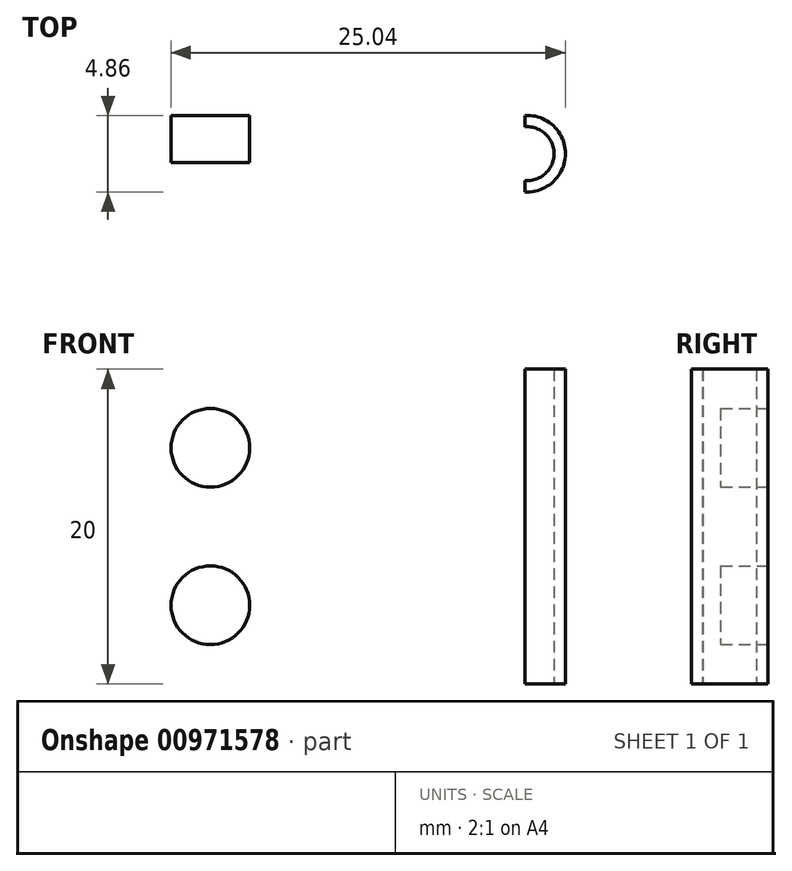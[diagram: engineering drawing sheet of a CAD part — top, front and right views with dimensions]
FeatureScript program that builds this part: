
annotation { "Feature Type Name" : "Feature", "Feature Type Description" : "" }
export const myFeature = defineFeature(function(context is Context, id is Id, definition is map)
    precondition{}
    {
        {
            var Q0;
            Q0=qCreatedBy(makeId("Top.planeOp"),FACE);
            var sketch = newSketch(context, id + "F0", { "sketchPlane" : qUnion([Q0])});
            skLineSegment(sketch, "E0", {"start": v(-27.53, 0) * mm, "end": v(-2.53, 0) * mm});
            skLineSegment(sketch, "E1", {"start": v(-27.53, 0) * mm, "end": v(-27.53, -3) * mm});
            skLineSegment(sketch, "E2", {"start": v(-27.53, -3) * mm, "end": v(-2.53, -3) * mm});
            skLineSegment(sketch, "E3", {"start": v(-2.53, -3) * mm, "end": v(-2.53, 0) * mm});
            skCircle(sketch, "E4", {"center": v(-2.67, -2.43) * mm, "radius": 2.43 * mm});
            skPoint(sketch, "E4.second.point", {"position": v(-2.53, -4.85) * mm});
            skPoint(sketch, "E4.third.point", {"position": v(-0.3, -3) * mm});
            skCircle(sketch, "E5", {"center": v(-2.67, -2.43) * mm, "radius": 1.71 * mm});
            skSolve(sketch);
        }
        {
            var Q0;
            {var subQ0=sQuery(id+"F0.wireOp",EDGE,"E4");var subQ1=sQuery(id+"F0.wireOp",EDGE,"E0");var subQ3=makeQuery(id+"F0.imprint","INTERSECT",VERTEX,{"derivedFrom":[subQ1,subQ0]});Q0=makeQuery(id+"F0.imprint","IMPRINT",FACE,{"disambiguationData":[TD([[makeQuery(id+"F0.imprint","IMPRINT",EDGE,{"disambiguationData":[TD([[subQ3,-1.0]])],"derivedFrom":subQ1}),1.0]])]});}
            var Q1;
            {var subQ0=sQuery(id+"F0.wireOp",EDGE,"E4");var subQ1=sQuery(id+"F0.wireOp",EDGE,"E2");var subQ2=makeQuery(id+"F0.imprint","INTERSECT",VERTEX,{"derivedFrom":[subQ1,subQ0]});Q1=makeQuery(id+"F0.imprint","IMPRINT",FACE,{"disambiguationData":[TD([[makeQuery(id+"F0.imprint","IMPRINT",EDGE,{"disambiguationData":[TD([[subQ2,-1.0]])],"derivedFrom":subQ1}),-1.0]])]});}
            var Q2;
            {var subQ0=sQuery(id+"F0.wireOp",EDGE,"E4");var subQ7=sQuery(id+"F0.wireOp",EDGE,"E2");var subQ8=makeQuery(id+"F0.imprint","INTERSECT",VERTEX,{"derivedFrom":[subQ7,subQ0]});Q2=makeQuery(id+"F0.imprint","IMPRINT",FACE,{"disambiguationData":[TD([[makeQuery(id+"F0.imprint","IMPRINT",EDGE,{"disambiguationData":[TD([[subQ8,-1.0]])],"derivedFrom":subQ7}),1.0]])]});}
            var Q3;
            {var subQ0=sQuery(id+"F0.wireOp",EDGE,"E1");Q3=makeQuery(id+"F0.imprint","IMPRINT",FACE,{"disambiguationData":[TD([[makeQuery(id+"F0.imprint","IMPRINT",EDGE,{"derivedFrom":subQ0}),1.0]])]});}
            extrude(context, id + "F1", {"entities" : qUnion([Q0, Q1, Q2, Q3]), "depth" : 20 * mm, "offsetDistance" : 25 * mm});
        }
        {
            var Q0;
            Q0=makeQuery(id+"F1.opExtrude","SWEPT_FACE",FACE,{"disambiguationData":[OSD([sQuery(id+"F0.wireOp",EDGE,"E0")])]});
            var sketch = newSketch(context, id + "F2", { "sketchPlane" : qUnion([Q0])});
            skLineSegment(sketch, "E6", {"start": v(22.78, 0) * mm, "end": v(22.78, 20) * mm});
            skLineSegment(sketch, "E7", {"start": v(22.78, 20) * mm, "end": v(22.78, 15) * mm});
            skLineSegment(sketch, "E8", {"start": v(22.78, 0) * mm, "end": v(22.78, 5) * mm});
            skCircle(sketch, "E9", {"center": v(22.78, 5) * mm, "radius": 2.5 * mm});
            skCircle(sketch, "E10", {"center": v(22.78, 15) * mm, "radius": 2.5 * mm});
            skSolve(sketch);
        }
        {
            var Q0;
            {var subQ0=sQuery(id+"F2.wireOp",EDGE,"E8");var subQ1=sQuery(id+"F2.wireOp",EDGE,"E6");var subQ2=makeQuery(id+"F2.imprint","INTERSECT",VERTEX,{"derivedFrom":[subQ1,subQ0]});Q0=makeQuery(id+"F2.imprint","IMPRINT",FACE,{"disambiguationData":[TD([[makeQuery(id+"F2.imprint","IMPRINT",EDGE,{"disambiguationData":[TD([[subQ2,-1.0]])],"derivedFrom":subQ1}),-1.0]])]});}
            var Q1;
            {var subQ0=sQuery(id+"F2.wireOp",EDGE,"E7");var subQ1=sQuery(id+"F2.wireOp",EDGE,"E6");var subQ2=makeQuery(id+"F2.imprint","INTERSECT",VERTEX,{"derivedFrom":[subQ1,subQ0]});Q1=makeQuery(id+"F2.imprint","IMPRINT",FACE,{"disambiguationData":[TD([[makeQuery(id+"F2.imprint","IMPRINT",EDGE,{"disambiguationData":[TD([[subQ2,1.0]])],"derivedFrom":subQ1}),-1.0]])]});}
            var Q2;
            {var subQ0=sQuery(id+"F2.wireOp",EDGE,"E7");var subQ1=sQuery(id+"F2.wireOp",EDGE,"E6");var subQ2=makeQuery(id+"F2.imprint","INTERSECT",VERTEX,{"derivedFrom":[subQ1,subQ0]});Q2=makeQuery(id+"F2.imprint","IMPRINT",FACE,{"disambiguationData":[TD([[makeQuery(id+"F2.imprint","IMPRINT",EDGE,{"disambiguationData":[TD([[subQ2,1.0]])],"derivedFrom":subQ1}),1.0]])]});}
            extrude(context, id + "F3", {"entities" : qUnion([Q0, Q1, Q2]), "operationType" : NewBodyOperationType.REMOVE, "oppositeDirection" : true, "depth" : 25 * mm, "offsetDistance" : 25 * mm});
        }
        {
            var Q0;
            {var subQ0=sQuery(id+"F2.wireOp",EDGE,"E8");var subQ1=sQuery(id+"F2.wireOp",EDGE,"E6");var subQ2=makeQuery(id+"F2.imprint","INTERSECT",VERTEX,{"derivedFrom":[subQ1,subQ0]});Q0=makeQuery(id+"F2.imprint","IMPRINT",FACE,{"disambiguationData":[TD([[makeQuery(id+"F2.imprint","IMPRINT",EDGE,{"disambiguationData":[TD([[subQ2,-1.0]])],"derivedFrom":subQ1}),1.0]])]});}
            extrude(context, id + "F4", {"entities" : qUnion([Q0]), "operationType" : NewBodyOperationType.REMOVE, "oppositeDirection" : true, "depth" : 25 * mm, "offsetDistance" : 25 * mm});
        }
    });
